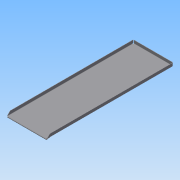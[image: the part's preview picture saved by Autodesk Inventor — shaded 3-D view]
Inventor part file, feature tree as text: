
AUTODESK INVENTOR PART (.ipt)
format: ipt  version: 2016 (Build 200138000, 138)  size: 186,368 bytes
history: native  units: mm
features: other x8, sketch x4, extrude x1
ambient origin geometry x8: Origin, YZ Plane, XZ Plane, XY Plane, X Axis, Y Axis, Z Axis, Center Point
bodies: Volumenkörper1 (feature_tree)
feature tree (13):
  other  "Fläche1"
  other  "Lasche1"
  other  "Falz1"
  extrude  "Extrusion1"  Depth=60.0mm
  sketch  "Skizze1"  dims[d0=60.0mm d1=190.0mm]
  other  "Grobblech1"
  sketch  "Skizze2"  dims[d2=0.5mm]
  other  "Grobblech2"
  other  "Biegung1"
  other  "Ecke1"
  sketch  "Skizze4"  dims[d4=0.25mm d5=1.0mm d6=0.5mm d7=5.0mm d8=90.0deg d9=0.5mm d10=2.0mm d11=0.5mm d12=0.5mm d13=0.5mm d14=0.25mm d15=1.0mm d16=0.5mm d20=33.161256mm d21=0.5mm d22=0.5mm d23=45.0deg d24=10.0mm d25=0.0mm]
  sketch  "Skizze3"  dims[d3=0.5mm]
  other  "Definition1"
